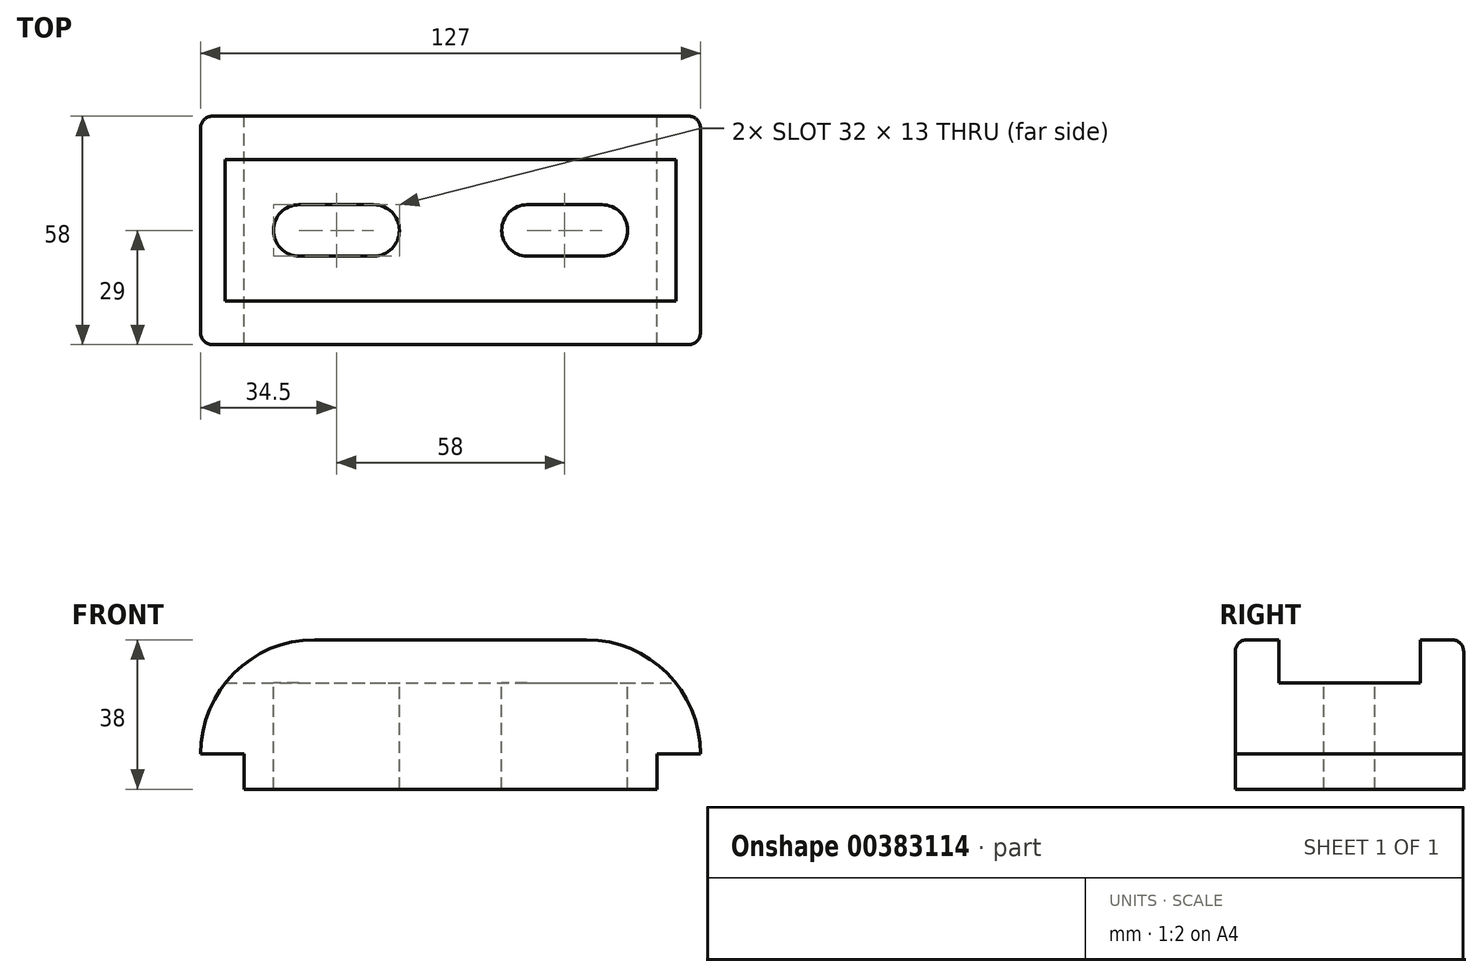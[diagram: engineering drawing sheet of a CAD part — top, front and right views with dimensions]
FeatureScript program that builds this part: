
annotation { "Feature Type Name" : "Feature", "Feature Type Description" : "" }
export const myFeature = defineFeature(function(context is Context, id is Id, definition is map)
    precondition{}
    {
        {
            var Q0;
            Q0=qCreatedBy(makeId("Front.planeOp"),FACE);
            var sketch = newSketch(context, id + "F0", { "sketchPlane" : qUnion([Q0])});
            skLineSegment(sketch, "E0", {"start": v(0, 0) * mm, "end": v(52.5, 0) * mm});
            skLineSegment(sketch, "E1", {"start": v(52.5, 0) * mm, "end": v(52.5, 9) * mm});
            skLineSegment(sketch, "E2", {"start": v(52.5, 9) * mm, "end": v(63.5, 9) * mm});
            skArc(sketch, "E3", {"start": v(63.5, 9) * mm, "mid": v(55, 29.5) * mm, "end": v(34.5, 38) * mm});
            skLineSegment(sketch, "E4", {"start": v(34.5, 38) * mm, "end": v(0, 38) * mm});
            skArc(sketch, "E5.MirrorCS", {"start": v(-63.5, 9) * mm, "mid": v(-55, 29.5) * mm, "end": v(-34.5, 38) * mm});
            skLineSegment(sketch, "E6.MirrorCS", {"start": v(-34.5, 38) * mm, "end": v(0, 38) * mm});
            skLineSegment(sketch, "E7.MirrorCS", {"start": v(0, 0) * mm, "end": v(-52.5, 0) * mm});
            skLineSegment(sketch, "E8.MirrorCS", {"start": v(-52.5, 9) * mm, "end": v(-63.5, 9) * mm});
            skLineSegment(sketch, "E9.MirrorCS", {"start": v(-52.5, 0) * mm, "end": v(-52.5, 9) * mm});
            skSolve(sketch);
        }
        {
            var Q0;
            Q0 = qSketchRegion(id + "F0", true);
            extrude(context, id + "F1", {"entities" : qUnion([Q0]), "endBound" : BoundingType.SYMMETRIC, "depth" : 58 * mm});
        }
        {
            var Q0;
            Q0=qCreatedBy(makeId("Right.planeOp"),FACE);
            var sketch = newSketch(context, id + "F2", { "sketchPlane" : qUnion([Q0])});
            skLineSegment(sketch, "E10.bottom", {"start": v(-18, 38) * mm, "end": v(18, 38) * mm});
            skLineSegment(sketch, "E10.top", {"start": v(-18, 27) * mm, "end": v(18, 27) * mm});
            skLineSegment(sketch, "E10.left", {"start": v(-18, 38) * mm, "end": v(-18, 27) * mm});
            skLineSegment(sketch, "E10.right", {"start": v(18, 38) * mm, "end": v(18, 27) * mm});
            skSolve(sketch);
        }
        {
            var Q0;
            Q0 = qSketchRegion(id + "F2", true);
            extrude(context, id + "F3", {"entities" : qUnion([Q0]), "operationType" : NewBodyOperationType.REMOVE, "endBound" : BoundingType.THROUGH_ALL, "oppositeDirection" : true, "depth" : 200 * mm, "hasSecondDirection" : true, "secondDirectionBound" : SecondDirectionBoundingType.THROUGH_ALL, "secondDirectionOppositeDirection" : false, "secondDirectionDepth" : 25 * mm});
        }
        {
            var Q0;
            Q0=makeQuery(id+"F3.boolean.opBoolean","COPY",FACE,{"derivedFrom":makeQuery(id+"F3.opExtrude","SWEPT_FACE",FACE,{"disambiguationData":[OSD([sQuery(id+"F2.wireOp",EDGE,"E10.top")])]})});
            var sketch = newSketch(context, id + "F4", { "sketchPlane" : qUnion([Q0])});
            skArc(sketch, "E11", {"start": v(-38.5, 6.5) * mm, "mid": v(-45, 0) * mm, "end": v(-38.5, -6.5) * mm});
            skArc(sketch, "E12", {"start": v(-19.5, -6.5) * mm, "mid": v(-13, 0) * mm, "end": v(-19.5, 6.5) * mm});
            skArc(sketch, "E13", {"start": v(19.5, 6.5) * mm, "mid": v(13, 0) * mm, "end": v(19.5, -6.5) * mm});
            skArc(sketch, "E14", {"start": v(38.5, -6.5) * mm, "mid": v(45, 0) * mm, "end": v(38.5, 6.5) * mm});
            skLineSegment(sketch, "E15", {"start": v(-38.5, -6.5) * mm, "end": v(-19.5, -6.5) * mm});
            skLineSegment(sketch, "E16", {"start": v(-38.5, 6.5) * mm, "end": v(-19.5, 6.5) * mm});
            skLineSegment(sketch, "E17", {"start": v(19.5, -6.5) * mm, "end": v(38.5, -6.5) * mm});
            skLineSegment(sketch, "E18", {"start": v(19.5, 6.5) * mm, "end": v(38.5, 6.5) * mm});
            skSolve(sketch);
        }
        {
            var Q0;
            Q0=makeQuery(id+"F4.imprint","IMPRINT",FACE,{"disambiguationData":[TD([[makeQuery(id+"F4.imprint","IMPRINT",EDGE,{"derivedFrom":sQuery(id+"F4.wireOp",EDGE,"E11")}),1.0]])]});
            var Q1;
            Q1=makeQuery(id+"F4.imprint","IMPRINT",FACE,{"disambiguationData":[TD([[makeQuery(id+"F4.imprint","IMPRINT",EDGE,{"derivedFrom":sQuery(id+"F4.wireOp",EDGE,"E13")}),1.0]])]});
            extrude(context, id + "F5", {"entities" : qUnion([Q0, Q1]), "operationType" : NewBodyOperationType.REMOVE, "endBound" : BoundingType.THROUGH_ALL, "oppositeDirection" : true, "depth" : 25 * mm});
        }
        {
            var Q0;
            Q0=makeQuery(id+"F1.opExtrude","CAP_EDGE",EDGE,{"disambiguationData":[OSD([sQuery(id+"F0.wireOp",EDGE,"E4"),sQuery(id+"F0.wireOp",EDGE,"E6.MirrorCS")])],"isStart":false});
            var Q1;
            Q1=makeQuery(id+"F1.opExtrude","CAP_EDGE",EDGE,{"disambiguationData":[OSD([sQuery(id+"F0.wireOp",EDGE,"E4"),sQuery(id+"F0.wireOp",EDGE,"E6.MirrorCS")])],"isStart":true});
            fillet(context, id + "F6", {"entities" : qUnion([Q0, Q1]), "radius" : 3 * mm, "tangentPropagation" : true, "allowEdgeOverflow" : false});
        }
    });
